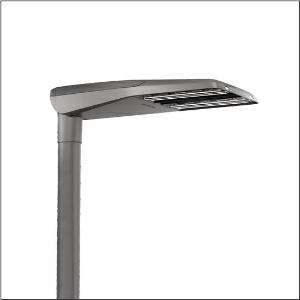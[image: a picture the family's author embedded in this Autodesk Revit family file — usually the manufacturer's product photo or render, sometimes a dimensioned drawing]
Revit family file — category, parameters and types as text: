
# Revit family: streetlight_sl_11_iq_midi___pc-r_5xc3f21f08me_be3f
name_source: partatom
category: Lighting Fixtures
units: mm (PartAtom-declared; Revit-internal decimal feet)

## family parameters
Cut with Voids When Loaded = No
Host = Face
Light Source = No
Part Type = Normal
Room Calculation Point = No
Round Connector Dimension = Use Diameter
Shared = No

## types (1)
- --- (1 x LED, 12740 lm, 124.7 W, 2200K)
    Apparent Load = 125 VA
    CIE Flux Codes = 37 73 96 100 100
    Color Rendering = 70
    Color Temperature = 2200K
    Default Elevation = 1800 mm
    Description = Streetlight SL 11 iQ midi, mast luminaire, primary light control with 3 zone facetted reflector, of plastic, silver coated, highly specular, primary optical cover: cover, of PMMA, transparent, light distribution: PC-R, light emission: direct distribution, primary light characteristic: asymmetric, right, installation type: post-top, side-entry, LED, High Power LED, rated luminous flux: 12.740lm, luminous efficacy: 102lm/W, light colour: 722, colour temperature: 2200K, control: Street-Remote, optimised constant luminous flux control (CLO 2.0), Desk-Remote (wireless, voltage-free reading and setting of iQ features in the workshop via application-optimized NFC function/RFID function), Light-Fading, Smart-Wire, Night-Set, Lumen-Switch, Temp-Guard, Auto-Match, with cable H07RN-F 5x 1.5mm², mains connection: 230..240V, AC, 50/60Hz, connection cable pre-assembled, cable length: 12,5m, start of lifetime: 125W, end of service life: 132W, reduction: 57W, luminaire housing, of diecast aluminium, powder-coated, Siteco® metallic grey (DB 702S), please order mast flange separately, inclination adjustable without tools: 0°, 5°, 10°, 15° (post-top) | 0°, -5°, -10°, -15° (side-entry), sealing non-destructively replaceable, multi-level sealing system, length: 780mm, width: 376mm, height: 118mm, mast flange for spigot size: 42mm (side-entry): 5XC10008XM4, 60/48mm (side-entry/post-top): 5XC10108XM2, 76/60mm (side-entry/post-top): 5XC10108XM1, equipment: Power, protection rating (complete): IP66, insulation class (complete): insulation class II (safety insulation), certification: CE, ENEC, VDE, impact resistance: IK09, permissible operating ambient temperature for outdoor applications: -25..+50°C, standard-compliant lighting for roads and squares, Environmental Product Declaration (EPD) tested and certified by an independent institute, packaging unit: 1 piece

Light Distribution: PC-R
    Height = 118 mm
    Lamp = 1 x LED
    Lamp Light Flux = 12740 lm
    Lamp Power = 124.7 W
    Lamp count = 1
    Length = 780 mm
    Luminous efficacy = 102 lm/W
    Manufacturer = Siteco
    ModVariant = No
    Model = 5XC3F21F08ME
    Number of Poles = 1
    OnlyDefault = Yes
    Power Factor = 1
    Product Name = Streetlight SL 11 iQ midi | PC-R
    Product group = mast luminaire | pylon top
    ProductGroupID = 6100
    Protection Class = Protection class II
    Protection Degree = IP 66
    RLX_Detail_Level = 1
    RLX_Emergency_Light_Flux = 0 lm
    RLX_Emergency_Type = 0
    RLX_Emergency_Type_DB = No
    RlxData = <blob elided: 74269 chars, md5=d1713ca4>
    Socket = socket
    Standby Power = 0 W
    System Light Flux = 12741 lm
    System Power = 125 W
    Type Comments = factory setting: luminous flux: 100 % | dim-lin: 254 | 557 mA
    Type Image = l_1005960.jpg
    URL = http://relux.com
    VarID = @adj_096955
    Voltage = 0 V
    Weight = 0.00 kg
    Width = 376 mm

## geometry (parser evidence)
native form markers: Blend x4, Sweep x12
no freeform markers — native parametric forms only
